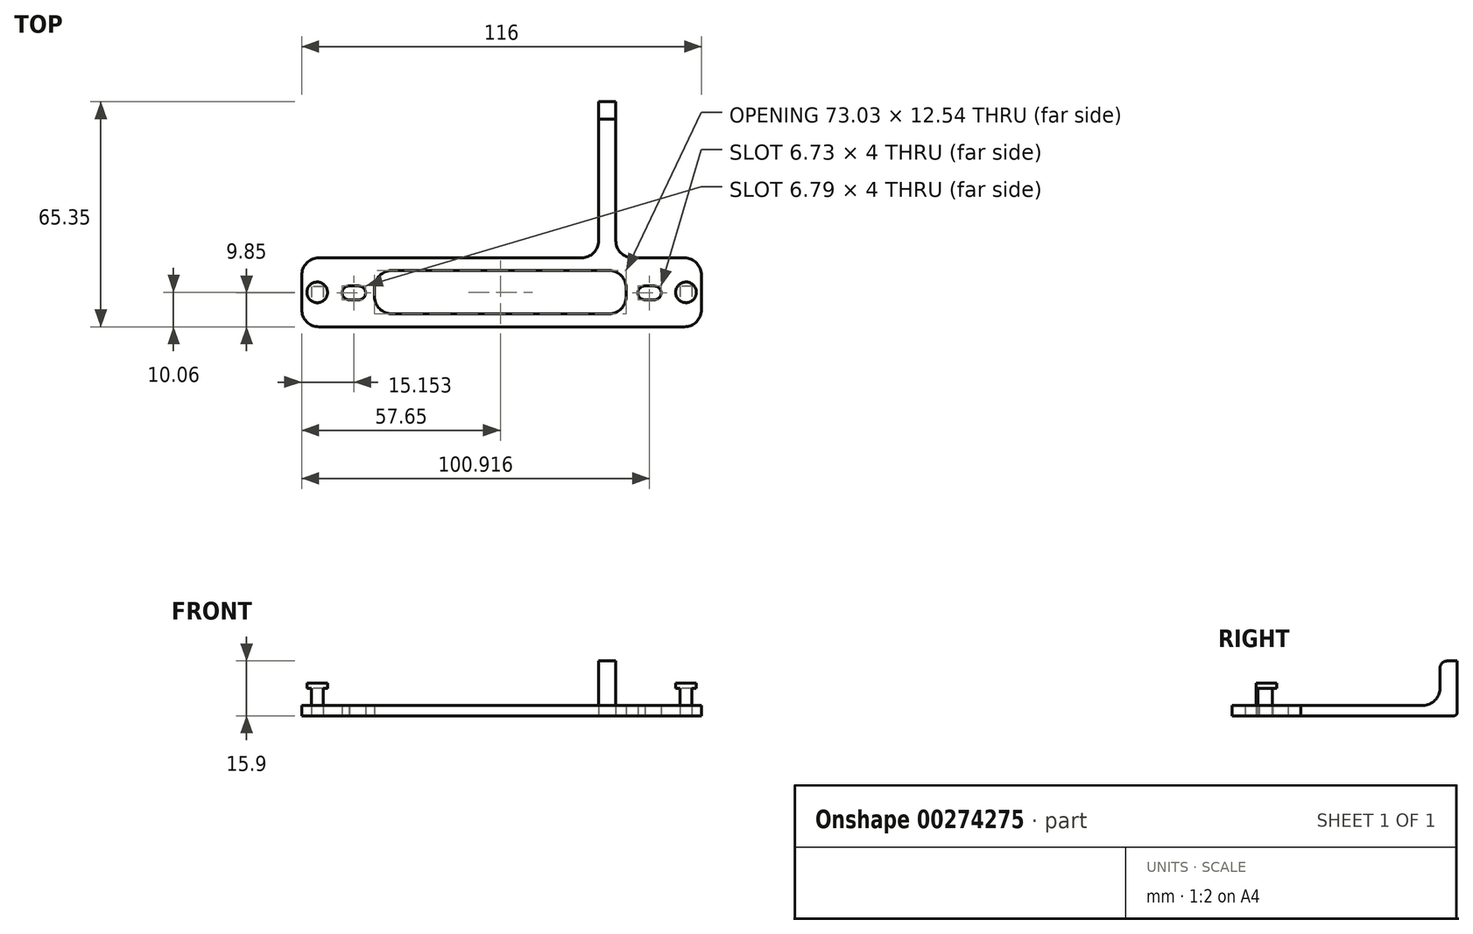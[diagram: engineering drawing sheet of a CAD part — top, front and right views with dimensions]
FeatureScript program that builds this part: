
annotation { "Feature Type Name" : "Feature", "Feature Type Description" : "" }
export const myFeature = defineFeature(function(context is Context, id is Id, definition is map)
    precondition{}
    {
        {
            var Q0;
            Q0=qCreatedBy(makeId("Top.planeOp"),FACE);
            var sketch = newSketch(context, id + "F0", { "sketchPlane" : qUnion([Q0])});
            skLineSegment(sketch, "E0.bottom", {"start": v(-58.05, 10.15) * mm, "end": v(57.95, 10.15) * mm});
            skLineSegment(sketch, "E0.top", {"start": v(-58.05, -9.85) * mm, "end": v(57.95, -9.85) * mm});
            skLineSegment(sketch, "E0.left", {"start": v(-58.05, 10.15) * mm, "end": v(-58.05, -9.85) * mm});
            skLineSegment(sketch, "E0.right", {"start": v(57.95, 10.15) * mm, "end": v(57.95, -9.85) * mm});
            skLineSegment(sketch, "E1", {"start": v(-0.05, 10.15) * mm, "end": v(-0.05, -9.85) * mm, "construction": true});
            skLineSegment(sketch, "E2", {"start": v(53.45, 10.15) * mm, "end": v(53.45, -9.85) * mm, "construction": true});
            skLineSegment(sketch, "E3", {"start": v(-53.55, 10.15) * mm, "end": v(-53.55, -9.85) * mm, "construction": true});
            skCircle(sketch, "E4", {"center": v(53.45, 0.15) * mm, "radius": 3 * mm});
            skCircle(sketch, "E5", {"center": v(-53.55, 0.15) * mm, "radius": 3 * mm});
            skLineSegment(sketch, "E6", {"start": v(-46.3, 10.15) * mm, "end": v(-46.3, -9.85) * mm, "construction": true});
            skLineSegment(sketch, "E7", {"start": v(46.2, 10.15) * mm, "end": v(46.2, -9.85) * mm, "construction": true});
            skLineSegment(sketch, "E8", {"start": v(-39.5, 10.15) * mm, "end": v(-39.5, -9.85) * mm, "construction": true});
            skLineSegment(sketch, "E9", {"start": v(39.5, 10.15) * mm, "end": v(39.5, -9.85) * mm, "construction": true});
            skCircle(sketch, "E10", {"center": v(-44.3, 0) * mm, "radius": 2 * mm});
            skCircle(sketch, "E11", {"center": v(44.23, 0) * mm, "radius": 2 * mm});
            skCircle(sketch, "E12", {"center": v(-41.5, 0) * mm, "radius": 2 * mm});
            skCircle(sketch, "E13", {"center": v(41.5, 0) * mm, "radius": 2 * mm});
            skLineSegment(sketch, "E14", {"start": v(-44.23, 2) * mm, "end": v(-41.5, 2) * mm});
            skLineSegment(sketch, "E15", {"start": v(-44.46, -2) * mm, "end": v(-41.5, -2) * mm});
            skLineSegment(sketch, "E16", {"start": v(41.42, 2) * mm, "end": v(44.23, 2) * mm});
            skLineSegment(sketch, "E17", {"start": v(41.53, -2) * mm, "end": v(44.23, -2) * mm});
            skLineSegment(sketch, "E18.bottom", {"start": v(28.1, 0) * mm, "end": v(33.1, 0) * mm});
            skLineSegment(sketch, "E18.top", {"start": v(28.1, 50.5) * mm, "end": v(33.1, 50.5) * mm});
            skLineSegment(sketch, "E18.left", {"start": v(28.1, 0) * mm, "end": v(28.1, 50.5) * mm});
            skLineSegment(sketch, "E18.right", {"start": v(33.1, 0) * mm, "end": v(33.1, 50.5) * mm});
            skLineSegment(sketch, "E19.top", {"start": v(28.1, 55.5) * mm, "end": v(33.1, 55.5) * mm});
            skLineSegment(sketch, "E19.left", {"start": v(28.1, 50.5) * mm, "end": v(28.1, 55.5) * mm});
            skLineSegment(sketch, "E19.right", {"start": v(33.1, 50.5) * mm, "end": v(33.1, 55.5) * mm});
            skLineSegment(sketch, "E20.bottom", {"start": v(-36.92, 6.48) * mm, "end": v(36.11, 6.48) * mm});
            skLineSegment(sketch, "E20.top", {"start": v(-36.92, -6.06) * mm, "end": v(36.11, -6.06) * mm});
            skLineSegment(sketch, "E20.left", {"start": v(-36.92, 6.48) * mm, "end": v(-36.92, -6.06) * mm});
            skLineSegment(sketch, "E20.right", {"start": v(36.11, 6.48) * mm, "end": v(36.11, -6.06) * mm});
            skLineSegment(sketch, "E21", {"start": v(-55.25, 2.62) * mm, "end": v(-55.25, -2.32) * mm});
            skLineSegment(sketch, "E22", {"start": v(-51.75, 2.55) * mm, "end": v(-51.75, -2.25) * mm});
            skLineSegment(sketch, "E23", {"start": v(51.7, 2.58) * mm, "end": v(51.7, -2.29) * mm});
            skLineSegment(sketch, "E24", {"start": v(55.2, 2.59) * mm, "end": v(55.2, -2.29) * mm});
            skLineSegment(sketch, "E25", {"start": v(55.2, 1.9) * mm, "end": v(51.7, 1.9) * mm});
            skLineSegment(sketch, "E26", {"start": v(-51.75, 1.75) * mm, "end": v(-55.25, 1.75) * mm});
            skSolve(sketch);
        }
        {
            var Q0;
            Q0=makeQuery(id+"F0.imprint","IMPRINT",FACE,{"disambiguationData":[TD([[makeQuery(id+"F0.imprint","IMPRINT",EDGE,{"derivedFrom":sQuery(id+"F0.wireOp",EDGE,"E0.bottom")}),-1.0]])]});
            var Q1;
            Q1=makeQuery(id+"F0.imprint","IMPRINT",FACE,{"disambiguationData":[TD([[makeQuery(id+"F0.imprint","IMPRINT",EDGE,{"derivedFrom":sQuery(id+"F0.wireOp",EDGE,"E5")}),1.0]])]});
            var Q2;
            Q2=makeQuery(id+"F0.imprint","IMPRINT",FACE,{"disambiguationData":[TD([[makeQuery(id+"F0.imprint","IMPRINT",EDGE,{"derivedFrom":sQuery(id+"F0.wireOp",EDGE,"rC1dJ4SD-zf09-XqYZ-SrmD-UccuzO4AM2G4")}),1.0]])]});
            var Q3;
            Q3=makeQuery(id+"F0.imprint","IMPRINT",FACE,{"disambiguationData":[TD([[makeQuery(id+"F0.imprint","IMPRINT",EDGE,{"derivedFrom":sQuery(id+"F0.wireOp",EDGE,"E4")}),1.0]])]});
            var Q4;
            Q4=makeQuery(id+"F0.imprint","IMPRINT",FACE,{"disambiguationData":[TD([[makeQuery(id+"F0.imprint","IMPRINT",EDGE,{"derivedFrom":sQuery(id+"F0.wireOp",EDGE,"akhzGEth-cOzL-kwVj-vOwI-uBbZSS0Hw84j")}),1.0]])]});
            var Q5;
            {var subQ5=sQuery(id+"F0.wireOp",EDGE,"E18.top");Q5=makeQuery(id+"F0.imprint","IMPRINT",FACE,{"disambiguationData":[TD([[makeQuery(id+"F0.imprint","IMPRINT",EDGE,{"derivedFrom":subQ5}),-1.0]])]});}
            var Q6;
            Q6=makeQuery(id+"F0.imprint","IMPRINT",FACE,{"disambiguationData":[TD([[makeQuery(id+"F0.imprint","IMPRINT",EDGE,{"derivedFrom":sQuery(id+"F0.wireOp",EDGE,"E18.top")}),1.0]])]});
            var Q7;
            {var subQ0=sQuery(id+"F0.wireOp",EDGE,"E18.left");var subQ1=sQuery(id+"F0.wireOp",EDGE,"E0.bottom");var subQ2=makeQuery(id+"F0.imprint","INTERSECT",VERTEX,{"derivedFrom":[subQ1,subQ0]});Q7=makeQuery(id+"F0.imprint","IMPRINT",FACE,{"disambiguationData":[TD([[makeQuery(id+"F0.imprint","IMPRINT",EDGE,{"disambiguationData":[TD([[subQ2,-1.0]])],"derivedFrom":subQ1}),-1.0]])]});}
            var Q8;
            {var subQ0=sQuery(id+"F0.wireOp",EDGE,"E22");Q8=makeQuery(id+"F0.imprint","IMPRINT",FACE,{"disambiguationData":[TD([[makeQuery(id+"F0.imprint","IMPRINT",EDGE,{"derivedFrom":subQ0}),1.0]])]});}
            var Q9;
            {var subQ0=sQuery(id+"F0.wireOp",EDGE,"E21");Q9=makeQuery(id+"F0.imprint","IMPRINT",FACE,{"disambiguationData":[TD([[makeQuery(id+"F0.imprint","IMPRINT",EDGE,{"derivedFrom":subQ0}),-1.0]])]});}
            var Q10;
            {var subQ0=sQuery(id+"F0.wireOp",EDGE,"E24");Q10=makeQuery(id+"F0.imprint","IMPRINT",FACE,{"disambiguationData":[TD([[makeQuery(id+"F0.imprint","IMPRINT",EDGE,{"derivedFrom":subQ0}),1.0]])]});}
            var Q11;
            {var subQ0=sQuery(id+"F0.wireOp",EDGE,"E23");Q11=makeQuery(id+"F0.imprint","IMPRINT",FACE,{"disambiguationData":[TD([[makeQuery(id+"F0.imprint","IMPRINT",EDGE,{"derivedFrom":subQ0}),-1.0]])]});}
            var Q12;
            {var subQ5=sQuery(id+"F0.wireOp",EDGE,"E25");Q12=makeQuery(id+"F0.imprint","IMPRINT",FACE,{"disambiguationData":[TD([[makeQuery(id+"F0.imprint","IMPRINT",EDGE,{"derivedFrom":subQ5}),1.0]])]});}
            var Q13;
            {var subQ5=sQuery(id+"F0.wireOp",EDGE,"E25");Q13=makeQuery(id+"F0.imprint","IMPRINT",FACE,{"disambiguationData":[TD([[makeQuery(id+"F0.imprint","IMPRINT",EDGE,{"derivedFrom":subQ5}),-1.0]])]});}
            var Q14;
            {var subQ5=sQuery(id+"F0.wireOp",EDGE,"E26");Q14=makeQuery(id+"F0.imprint","IMPRINT",FACE,{"disambiguationData":[TD([[makeQuery(id+"F0.imprint","IMPRINT",EDGE,{"derivedFrom":subQ5}),-1.0]])]});}
            var Q15;
            {var subQ5=sQuery(id+"F0.wireOp",EDGE,"E26");Q15=makeQuery(id+"F0.imprint","IMPRINT",FACE,{"disambiguationData":[TD([[makeQuery(id+"F0.imprint","IMPRINT",EDGE,{"derivedFrom":subQ5}),1.0]])]});}
            extrude(context, id + "F1", {"entities" : qUnion([Q0, Q1, Q2, Q3, Q4, Q5, Q6, Q7, Q8, Q9, Q10, Q11, Q12, Q13, Q14, Q15]), "depth" : 3 * mm});
        }
        {
            var Q0;
            {var subQ5=sQuery(id+"F0.wireOp",EDGE,"E25");Q0=makeQuery(id+"F0.imprint","IMPRINT",FACE,{"disambiguationData":[TD([[makeQuery(id+"F0.imprint","IMPRINT",EDGE,{"derivedFrom":subQ5}),1.0]])]});}
            var Q1;
            {var subQ5=sQuery(id+"F0.wireOp",EDGE,"E26");Q1=makeQuery(id+"F0.imprint","IMPRINT",FACE,{"disambiguationData":[TD([[makeQuery(id+"F0.imprint","IMPRINT",EDGE,{"derivedFrom":subQ5}),1.0]])]});}
            extrude(context, id + "F2", {"entities" : qUnion([Q0, Q1]), "depth" : 8 * mm});
        }
        {
            var Q0;
            {var subQ0=sQuery(id+"F0.wireOp",EDGE,"E21");Q0=makeQuery(id+"F0.imprint","IMPRINT",FACE,{"disambiguationData":[TD([[makeQuery(id+"F0.imprint","IMPRINT",EDGE,{"derivedFrom":subQ0}),-1.0]])]});}
            var Q1;
            {var subQ0=sQuery(id+"F0.wireOp",EDGE,"E21");Q1=makeQuery(id+"F0.imprint","IMPRINT",FACE,{"disambiguationData":[TD([[makeQuery(id+"F0.imprint","IMPRINT",EDGE,{"derivedFrom":subQ0}),1.0]])]});}
            var Q2;
            {var subQ0=sQuery(id+"F0.wireOp",EDGE,"E22");Q2=makeQuery(id+"F0.imprint","IMPRINT",FACE,{"disambiguationData":[TD([[makeQuery(id+"F0.imprint","IMPRINT",EDGE,{"derivedFrom":subQ0}),1.0]])]});}
            var Q3;
            {var subQ0=sQuery(id+"F0.wireOp",EDGE,"E23");Q3=makeQuery(id+"F0.imprint","IMPRINT",FACE,{"disambiguationData":[TD([[makeQuery(id+"F0.imprint","IMPRINT",EDGE,{"derivedFrom":subQ0}),-1.0]])]});}
            var Q4;
            {var subQ0=sQuery(id+"F0.wireOp",EDGE,"E23");Q4=makeQuery(id+"F0.imprint","IMPRINT",FACE,{"disambiguationData":[TD([[makeQuery(id+"F0.imprint","IMPRINT",EDGE,{"derivedFrom":subQ0}),1.0]])]});}
            var Q5;
            {var subQ0=sQuery(id+"F0.wireOp",EDGE,"E24");Q5=makeQuery(id+"F0.imprint","IMPRINT",FACE,{"disambiguationData":[TD([[makeQuery(id+"F0.imprint","IMPRINT",EDGE,{"derivedFrom":subQ0}),1.0]])]});}
            extrude(context, id + "F3", {"entities" : qUnion([Q0, Q1, Q2, Q3, Q4, Q5]), "operationType" : NewBodyOperationType.ADD, "depth" : 9.5 * mm, "hasSecondDirection" : true, "secondDirectionOppositeDirection" : false, "secondDirectionDepth" : 8 * mm});
        }
        {
            var Q0;
            Q0=makeQuery(id+"F0.imprint","IMPRINT",FACE,{"disambiguationData":[TD([[makeQuery(id+"F0.imprint","IMPRINT",EDGE,{"derivedFrom":sQuery(id+"F0.wireOp",EDGE,"E18.top")}),1.0]])]});
            extrude(context, id + "F4", {"entities" : qUnion([Q0]), "operationType" : NewBodyOperationType.ADD, "depth" : 15.9 * mm});
        }
        {
            var Q0;
            Q0=makeQuery(id+"F1.opExtrude","SWEPT_EDGE",EDGE,{"disambiguationData":[OSD([sQuery(id+"F0.wireOp",EDGE,"E0.top"),sQuery(id+"F0.wireOp",EDGE,"E0.left")])]});
            var Q1;
            Q1=makeQuery(id+"F1.opExtrude","SWEPT_EDGE",EDGE,{"disambiguationData":[OSD([sQuery(id+"F0.wireOp",EDGE,"E0.top"),sQuery(id+"F0.wireOp",EDGE,"E0.right")])]});
            var Q2;
            Q2=makeQuery(id+"F1.opExtrude","SWEPT_EDGE",EDGE,{"disambiguationData":[OSD([sQuery(id+"F0.wireOp",EDGE,"E0.bottom"),sQuery(id+"F0.wireOp",EDGE,"E0.right")])]});
            var Q3;
            Q3=makeQuery(id+"F1.opExtrude","SWEPT_EDGE",EDGE,{"disambiguationData":[OSD([sQuery(id+"F0.wireOp",EDGE,"E0.bottom"),sQuery(id+"F0.wireOp",EDGE,"E0.left")])]});
            fillet(context, id + "F5", {"entities" : qUnion([Q0, Q1, Q2, Q3]), "radius" : 5 * mm, "tangentPropagation" : true, "allowEdgeOverflow" : false});
        }
        {
            var Q0;
            Q0=makeQuery(id+"F4.opExtrude","CAP_EDGE",EDGE,{"disambiguationData":[OSD([sQuery(id+"F0.wireOp",EDGE,"E18.top")])],"isStart":false});
            fillet(context, id + "F6", {"entities" : qUnion([Q0]), "radius" : 2 * mm, "tangentPropagation" : true, "allowEdgeOverflow" : false});
        }
        {
            var Q0;
            Q0=makeQuery(id+"F1.opExtrude","SWEPT_EDGE",EDGE,{"disambiguationData":[OSD([sQuery(id+"F0.wireOp",EDGE,"E20.bottom"),sQuery(id+"F0.wireOp",EDGE,"E20.left")])]});
            var Q1;
            Q1=makeQuery(id+"F1.opExtrude","SWEPT_EDGE",EDGE,{"disambiguationData":[OSD([sQuery(id+"F0.wireOp",EDGE,"E20.top"),sQuery(id+"F0.wireOp",EDGE,"E20.left")])]});
            var Q2;
            Q2=makeQuery(id+"F1.opExtrude","SWEPT_EDGE",EDGE,{"disambiguationData":[OSD([sQuery(id+"F0.wireOp",EDGE,"E20.top"),sQuery(id+"F0.wireOp",EDGE,"E20.right")])]});
            var Q3;
            Q3=makeQuery(id+"F1.opExtrude","SWEPT_EDGE",EDGE,{"disambiguationData":[OSD([sQuery(id+"F0.wireOp",EDGE,"E20.bottom"),sQuery(id+"F0.wireOp",EDGE,"E20.right")])]});
            var Q4;
            Q4=makeQuery(id+"F1.opExtrude","SWEPT_EDGE",EDGE,{"disambiguationData":[OSD([sQuery(id+"F0.wireOp",EDGE,"E0.bottom"),sQuery(id+"F0.wireOp",EDGE,"E18.left")])]});
            var Q5;
            Q5=makeQuery(id+"F1.opExtrude","SWEPT_EDGE",EDGE,{"disambiguationData":[OSD([sQuery(id+"F0.wireOp",EDGE,"E0.bottom"),sQuery(id+"F0.wireOp",EDGE,"E18.right")])]});
            fillet(context, id + "F7", {"entities" : qUnion([Q0, Q1, Q2, Q3, Q4, Q5]), "radius" : 5 * mm, "tangentPropagation" : true, "allowEdgeOverflow" : false});
        }
        {
            var Q0;
            Q0=makeQuery(id+"F4.boolean.opBoolean","INTERSECT",EDGE,{"derivedFrom":[makeQuery(id+"F1.opExtrude","CAP_FACE",FACE,{"disambiguationData":[OSD([sQuery(id+"F0.wireOp",EDGE,"E0.bottom"),sQuery(id+"F0.wireOp",EDGE,"E0.top"),sQuery(id+"F0.wireOp",EDGE,"E0.left"),sQuery(id+"F0.wireOp",EDGE,"E0.right"),sQuery(id+"F0.wireOp",EDGE,"E10"),sQuery(id+"F0.wireOp",EDGE,"E11"),sQuery(id+"F0.wireOp",EDGE,"E12"),sQuery(id+"F0.wireOp",EDGE,"E13"),sQuery(id+"F0.wireOp",EDGE,"E14"),sQuery(id+"F0.wireOp",EDGE,"E15"),sQuery(id+"F0.wireOp",EDGE,"E16"),sQuery(id+"F0.wireOp",EDGE,"E17"),sQuery(id+"F0.wireOp",EDGE,"E18.left"),sQuery(id+"F0.wireOp",EDGE,"E18.right"),sQuery(id+"F0.wireOp",EDGE,"E19.top"),sQuery(id+"F0.wireOp",EDGE,"E19.left"),sQuery(id+"F0.wireOp",EDGE,"E19.right"),sQuery(id+"F0.wireOp",EDGE,"E20.bottom"),sQuery(id+"F0.wireOp",EDGE,"E20.top"),sQuery(id+"F0.wireOp",EDGE,"E20.left"),sQuery(id+"F0.wireOp",EDGE,"E20.right")])],"isStart":false}),makeQuery(id+"F4.opExtrude","SWEPT_FACE",FACE,{"disambiguationData":[OSD([sQuery(id+"F0.wireOp",EDGE,"E18.top")])]})]});
            fillet(context, id + "F8", {"entities" : qUnion([Q0]), "radius" : 5 * mm, "tangentPropagation" : true, "allowEdgeOverflow" : false});
        }
        {
            var Q0;
            Q0=makeQuery(id+"F1.opExtrude","CAP_EDGE",EDGE,{"disambiguationData":[OSD([sQuery(id+"F0.wireOp",EDGE,"E19.top")])],"isStart":true});
            fillet(context, id + "F9", {"entities" : qUnion([Q0]), "radius" : 1 * mm, "tangentPropagation" : true, "allowEdgeOverflow" : false});
        }
    });
